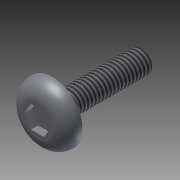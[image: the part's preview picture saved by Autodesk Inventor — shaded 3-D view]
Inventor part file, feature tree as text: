
AUTODESK INVENTOR PART (.ipt)
format: ipt  version: 2012 (Build 160160000, 160)  size: 120,320 bytes
history: native  units: in
note: dims shown in document units (in); Inventor stores cm internally (conversion verified against a paired STEP export)
features: extrude x3, sketch x1, thread x1, chamfer x1, fillet x1
ambient origin geometry x8: Origin, YZ Plane, XZ Plane, XY Plane, X Axis, Y Axis, Z Axis, Center Point
bodies: Solid1 (feature_tree)
feature tree (7):
  sketch  "Sketch1"  dims[d0=0.19in d1=0.5in d2=0.1875in d3=0.75in d4=0.0in d5=0.125in d6=0.0in d7=0.065in d8=0.0in d9=1.0in d10=0.0in d11=0.0156in d12=0.125in d13=45.0deg d14=0.125in]
  extrude  "Extrusion1"  Depth=0.5in
  extrude  "Extrusion2"  Depth=0.1875in
  extrude  "Extrusion3"  Depth=0.75in TaperAngle=0.0deg
  thread  "Thread1"  [1 undecoded]
  chamfer  "Chamfer1"  Distance=0.065in
  fillet  "Fillet1"  Radius=1.0in
note: 1 required parameter value undecoded (feature->parameter linkage not recoverable at this tier; creation-order binding heuristic only, values carry confidence <= 0.55)
